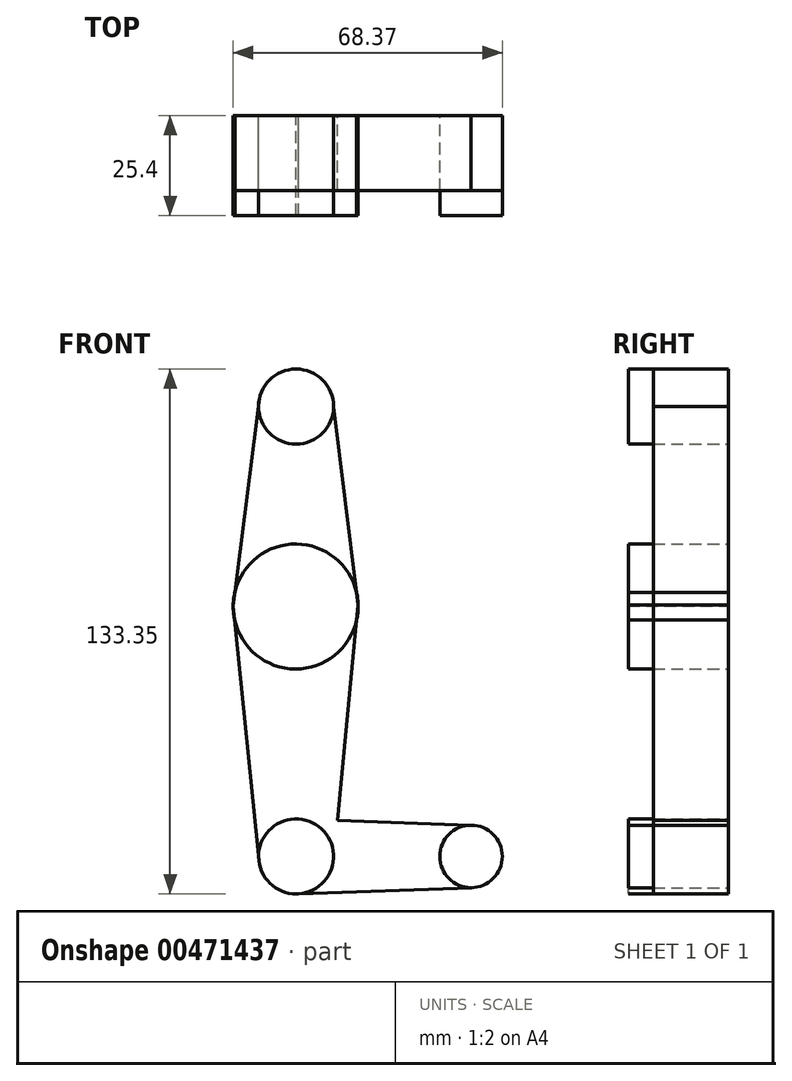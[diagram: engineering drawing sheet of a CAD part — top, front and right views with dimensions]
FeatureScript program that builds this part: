
annotation { "Feature Type Name" : "Feature", "Feature Type Description" : "" }
export const myFeature = defineFeature(function(context is Context, id is Id, definition is map)
    precondition{}
    {
        {
            var Q0;
            Q0=qCreatedBy(makeId("Front.planeOp"),FACE);
            var sketch = newSketch(context, id + "F0", { "sketchPlane" : qUnion([Q0])});
            skLineSegment(sketch, "E0", {"start": v(0, 40.38) * mm, "end": v(0, -73.92) * mm, "construction": true});
            skLineSegment(sketch, "E1", {"start": v(0, -73.92) * mm, "end": v(44.45, -73.92) * mm, "construction": true});
            skCircle(sketch, "E2", {"center": v(0, 40.38) * mm, "radius": 9.53 * mm});
            skCircle(sketch, "E3", {"center": v(-0.1, -10.42) * mm, "radius": 15.88 * mm});
            skCircle(sketch, "E4", {"center": v(0, -73.92) * mm, "radius": 9.53 * mm});
            skCircle(sketch, "E5", {"center": v(44.45, -73.92) * mm, "radius": 7.94 * mm});
            skLineSegment(sketch, "E6", {"start": v(-9.45, 41.56) * mm, "end": v(-15.98, -10.35) * mm});
            skLineSegment(sketch, "E7", {"start": v(-15.98, -10.35) * mm, "end": v(-9.48, -74.88) * mm});
            skLineSegment(sketch, "E8", {"start": v(44.45, -65.99) * mm, "end": v(0, -64.4) * mm});
            skLineSegment(sketch, "E9", {"start": v(0, -83.45) * mm, "end": v(44.73, -81.86) * mm});
            skLineSegment(sketch, "E10", {"start": v(9.52, 40.41) * mm, "end": v(15.77, -10.08) * mm});
            skLineSegment(sketch, "E11", {"start": v(15.77, -10.08) * mm, "end": v(9.57, -73.92) * mm});
            skSolve(sketch);
        }
        {
            var Q0;
            {var subQ0=sQuery(id+"F0.wireOp",EDGE,"E2");var subQ1=makeQuery(id+"F0.imprint","INTERSECT",VERTEX,{"derivedFrom":[subQ0,sQuery(id+"F0.wireOp",EDGE,"E6")]});Q0=makeQuery(id+"F0.imprint","IMPRINT",FACE,{"disambiguationData":[TD([[makeQuery(id+"F0.imprint","IMPRINT",EDGE,{"disambiguationData":[TD([[subQ1,1.0]])],"derivedFrom":subQ0}),1.0]])]});}
            var Q1;
            {var subQ2=sQuery(id+"F0.wireOp",EDGE,"E3");var subQ8=sQuery(id+"F0.wireOp",EDGE,"E10");var subQ9=makeQuery(id+"F0.imprint","INTERSECT",VERTEX,{"derivedFrom":[subQ2,subQ8]});Q1=makeQuery(id+"F0.imprint","IMPRINT",FACE,{"disambiguationData":[TD([[makeQuery(id+"F0.imprint","IMPRINT",EDGE,{"disambiguationData":[TD([[subQ9,-1.0]])],"derivedFrom":subQ2}),1.0]])]});}
            var Q2;
            {var subQ0=sQuery(id+"F0.wireOp",EDGE,"E4");var subQ1=makeQuery(id+"F0.imprint","INTERSECT",VERTEX,{"derivedFrom":[subQ0,sQuery(id+"F0.wireOp",EDGE,"E7")]});Q2=makeQuery(id+"F0.imprint","IMPRINT",FACE,{"disambiguationData":[TD([[makeQuery(id+"F0.imprint","IMPRINT",EDGE,{"disambiguationData":[TD([[subQ1,1.0]])],"derivedFrom":subQ0}),1.0]])]});}
            var Q3;
            {var subQ0=sQuery(id+"F0.wireOp",EDGE,"E5");var subQ1=makeQuery(id+"F0.imprint","INTERSECT",VERTEX,{"derivedFrom":[subQ0,sQuery(id+"F0.wireOp",EDGE,"E8")]});Q3=makeQuery(id+"F0.imprint","IMPRINT",FACE,{"disambiguationData":[TD([[makeQuery(id+"F0.imprint","IMPRINT",EDGE,{"disambiguationData":[TD([[subQ1,-1.0]])],"derivedFrom":subQ0}),1.0]])]});}
            extrude(context, id + "F1", {"entities" : qUnion([Q0, Q1, Q2, Q3]), "depth" : 25.4 * mm});
        }
        {
            var Q0;
            Q0 = qSketchRegion(id + "F0", true);
            extrude(context, id + "F2", {"entities" : qUnion([Q0]), "depth" : 19.05 * mm});
        }
    });
